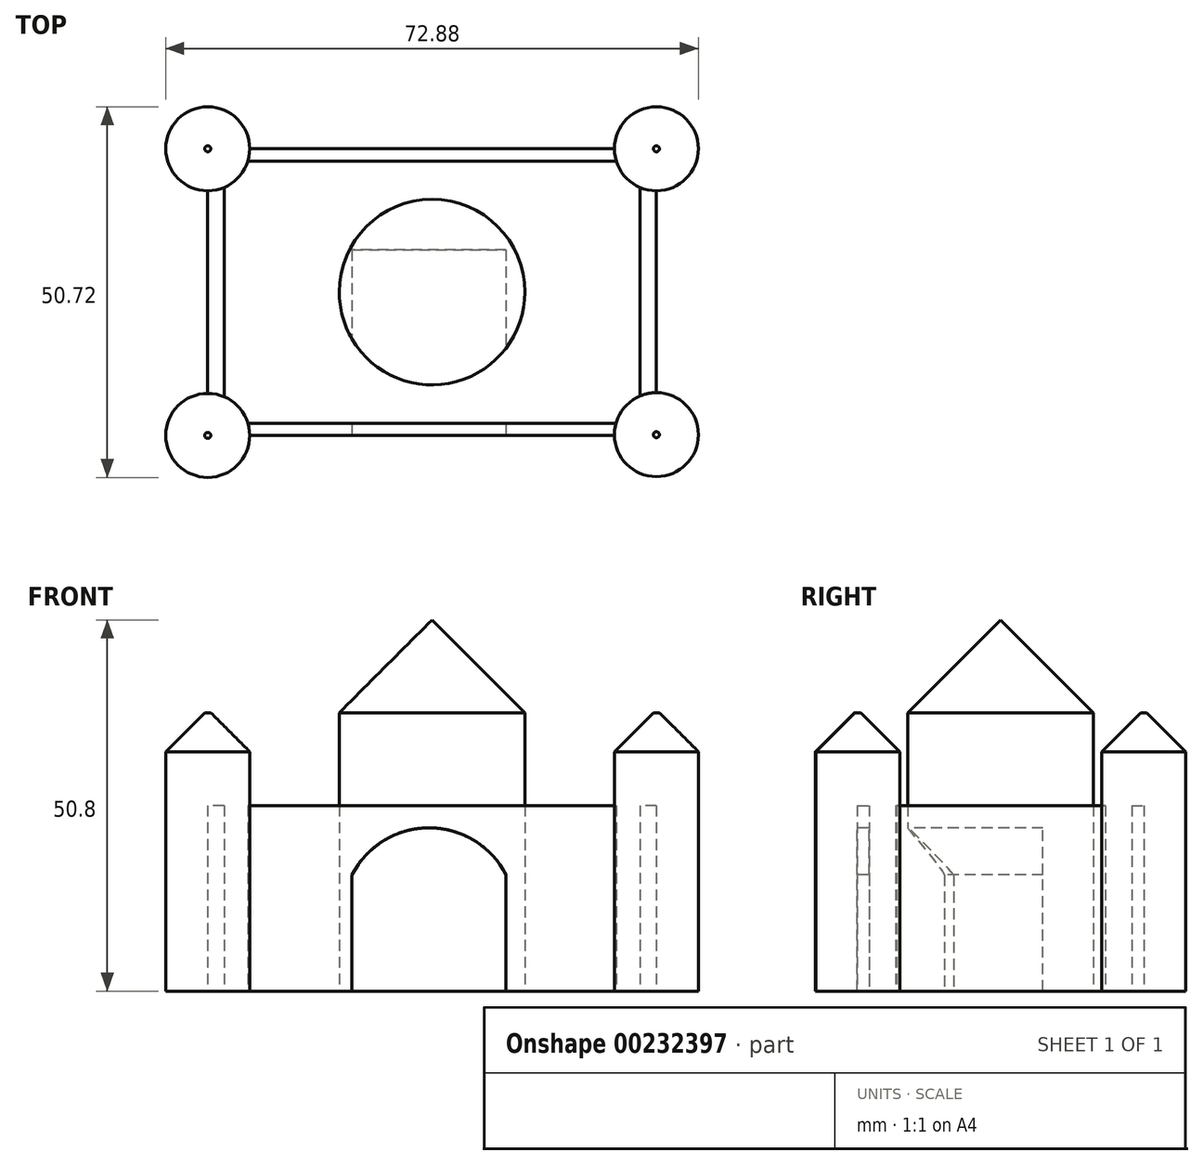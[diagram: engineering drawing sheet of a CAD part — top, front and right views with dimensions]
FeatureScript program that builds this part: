
annotation { "Feature Type Name" : "Feature", "Feature Type Description" : "" }
export const myFeature = defineFeature(function(context is Context, id is Id, definition is map)
    precondition{}
    {
        {
            var Q0;
            Q0=qCreatedBy(makeId("Top.planeOp"),FACE);
            var sketch = newSketch(context, id + "F0", { "sketchPlane" : qUnion([Q0])});
            skLineSegment(sketch, "E0.bottom", {"start": v(-24.95, -19.61) * mm, "end": v(24.95, -19.61) * mm});
            skLineSegment(sketch, "E0.top", {"start": v(-24.95, 19.61) * mm, "end": v(24.95, 19.61) * mm});
            skLineSegment(sketch, "E0.left", {"start": v(-30.7, -13.87) * mm, "end": v(-30.7, 13.87) * mm});
            skLineSegment(sketch, "E0.right", {"start": v(30.7, -19.61) * mm, "end": v(30.7, -19.52) * mm});
            skPoint(sketch, "E0.middle", {"position": v(0, 0) * mm});
            skCircle(sketch, "E1", {"center": v(0, 0) * mm, "radius": 12.7 * mm});
            skCircle(sketch, "E2", {"center": v(-30.7, 19.61) * mm, "radius": 5.75 * mm});
            skCircle(sketch, "E3", {"center": v(30.7, 19.61) * mm, "radius": 5.75 * mm});
            skCircle(sketch, "E4", {"center": v(30.7, -19.52) * mm, "radius": 5.75 * mm});
            skCircle(sketch, "E5", {"center": v(-30.7, -19.61) * mm, "radius": 5.75 * mm});
            skLineSegment(sketch, "E6.bottom", {"start": v(-25.2, -17.95) * mm, "end": v(25.17, -17.95) * mm});
            skLineSegment(sketch, "E6.top", {"start": v(-25.2, 17.95) * mm, "end": v(25.2, 17.95) * mm});
            skLineSegment(sketch, "E6.left", {"start": v(-28.44, -14.33) * mm, "end": v(-28.44, 14.33) * mm});
            skLineSegment(sketch, "E6.right", {"start": v(28.44, -14.23) * mm, "end": v(28.44, 14.33) * mm});
            skPoint(sketch, "E7.orphan", {"position": v(-28.44, -17.95) * mm});
            skLineSegment(sketch, "E8.trimOffspring", {"start": v(30.7, -13.77) * mm, "end": v(30.7, 13.87) * mm});
            skPoint(sketch, "E9.orphan", {"position": v(28.44, -17.95) * mm});
            skPoint(sketch, "E10.orphan", {"position": v(28.44, 17.95) * mm});
            skPoint(sketch, "E11.orphan", {"position": v(-28.44, 17.95) * mm});
            skSolve(sketch);
        }
        {
            var Q0;
            {var subQ0=sQuery(id+"F0.wireOp",EDGE,"E0.top");Q0=makeQuery(id+"F0.imprint","IMPRINT",FACE,{"disambiguationData":[TD([[makeQuery(id+"F0.imprint","IMPRINT",EDGE,{"derivedFrom":subQ0}),-1.0]])]});}
            var Q1;
            {var subQ0=sQuery(id+"F0.wireOp",EDGE,"E0.left");Q1=makeQuery(id+"F0.imprint","IMPRINT",FACE,{"disambiguationData":[TD([[makeQuery(id+"F0.imprint","IMPRINT",EDGE,{"derivedFrom":subQ0}),-1.0]])]});}
            var Q2;
            {var subQ0=sQuery(id+"F0.wireOp",EDGE,"E0.bottom");Q2=makeQuery(id+"F0.imprint","IMPRINT",FACE,{"disambiguationData":[TD([[makeQuery(id+"F0.imprint","IMPRINT",EDGE,{"derivedFrom":subQ0}),1.0]])]});}
            var Q3;
            {var subQ0=sQuery(id+"F0.wireOp",EDGE,"E6.right");Q3=makeQuery(id+"F0.imprint","IMPRINT",FACE,{"disambiguationData":[TD([[makeQuery(id+"F0.imprint","IMPRINT",EDGE,{"derivedFrom":subQ0}),-1.0]])]});}
            extrude(context, id + "F1", {"entities" : qUnion([Q0, Q1, Q2, Q3]), "depth" : 25.4 * mm});
        }
        {
            var Q0;
            {var subQ0=sQuery(id+"F0.wireOp",EDGE,"E2");var subQ1=makeQuery(id+"F0.imprint","INTERSECT",VERTEX,{"derivedFrom":[sQuery(id+"F0.wireOp",EDGE,"E0.top"),subQ0]});Q0=makeQuery(id+"F0.imprint","IMPRINT",FACE,{"disambiguationData":[TD([[makeQuery(id+"F0.imprint","IMPRINT",EDGE,{"disambiguationData":[TD([[subQ1,-1.0]])],"derivedFrom":subQ0}),1.0]])]});}
            var Q1;
            {var subQ0=sQuery(id+"F0.wireOp",EDGE,"E3");var subQ1=makeQuery(id+"F0.imprint","INTERSECT",VERTEX,{"derivedFrom":[sQuery(id+"F0.wireOp",EDGE,"E0.top"),subQ0]});Q1=makeQuery(id+"F0.imprint","IMPRINT",FACE,{"disambiguationData":[TD([[makeQuery(id+"F0.imprint","IMPRINT",EDGE,{"disambiguationData":[TD([[subQ1,-1.0]])],"derivedFrom":subQ0}),1.0]])]});}
            var Q2;
            {var subQ0=sQuery(id+"F0.wireOp",EDGE,"E5");var subQ1=makeQuery(id+"F0.imprint","INTERSECT",VERTEX,{"derivedFrom":[sQuery(id+"F0.wireOp",EDGE,"E0.bottom"),subQ0]});Q2=makeQuery(id+"F0.imprint","IMPRINT",FACE,{"disambiguationData":[TD([[makeQuery(id+"F0.imprint","IMPRINT",EDGE,{"disambiguationData":[TD([[subQ1,-1.0]])],"derivedFrom":subQ0}),1.0]])]});}
            var Q3;
            {var subQ0=sQuery(id+"F0.wireOp",EDGE,"E4");var subQ1=makeQuery(id+"F0.imprint","INTERSECT",VERTEX,{"derivedFrom":[subQ0,sQuery(id+"F0.wireOp",EDGE,"E6.right")]});Q3=makeQuery(id+"F0.imprint","IMPRINT",FACE,{"disambiguationData":[TD([[makeQuery(id+"F0.imprint","IMPRINT",EDGE,{"disambiguationData":[TD([[subQ1,1.0]])],"derivedFrom":subQ0}),1.0]])]});}
            extrude(context, id + "F2", {"entities" : qUnion([Q0, Q1, Q2, Q3]), "depth" : 38.1 * mm});
        }
        {
            var Q0;
            Q0=makeQuery(id+"F0.imprint","IMPRINT",FACE,{"disambiguationData":[TD([[makeQuery(id+"F0.imprint","IMPRINT",EDGE,{"derivedFrom":sQuery(id+"F0.wireOp",EDGE,"E1")}),1.0]])]});
            var Q1;
            Q1 = qSketchRegion(id + "F4", true);
            extrude(context, id + "F3", {"entities" : qUnion([Q0, Q1]), "depth" : 50.8 * mm});
        }
        {
            var Q0;
            Q0=makeQuery(id+"F1.opExtrude","SWEPT_FACE",FACE,{"disambiguationData":[OSD([sQuery(id+"F0.wireOp",EDGE,"E0.bottom")])]});
            var sketch = newSketch(context, id + "F4", { "sketchPlane" : qUnion([Q0])});
            skLineSegment(sketch, "E12.bottom", {"start": v(-10.96, 0) * mm, "end": v(10.13, 0) * mm});
            skLineSegment(sketch, "E12.left", {"start": v(-10.96, 0) * mm, "end": v(-10.96, 15.92) * mm});
            skLineSegment(sketch, "E12.right", {"start": v(10.13, 0) * mm, "end": v(10.13, 15.92) * mm});
            skArc(sketch, "E13", {"start": v(10.13, 15.92) * mm, "mid": v(-0.41, 22.34) * mm, "end": v(-10.96, 15.92) * mm});
            skSolve(sketch);
        }
        {
            var Q0;
            Q0 = qSketchRegion(id + "F4", true);
            extrude(context, id + "F5", {"entities" : qUnion([Q0]), "operationType" : NewBodyOperationType.REMOVE, "oppositeDirection" : true, "depth" : 25.4 * mm});
        }
        {
            var Q0;
            Q0=makeQuery(id+"F3.opExtrude","CAP_FACE",FACE,{"disambiguationData":[OSD([sQuery(id+"F0.wireOp",EDGE,"E1")])],"isStart":false});
            chamfer(context, id + "F6", {"entities" : qUnion([Q0]), "width" : 12.7 * mm, "tangentPropagation" : true});
        }
        {
            var Q0;
            Q0=makeQuery(id+"F2.opExtrude","CAP_FACE",FACE,{"disambiguationData":[OSD([sQuery(id+"F0.wireOp",EDGE,"E5")])],"isStart":false});
            var Q1;
            Q1=makeQuery(id+"F2.opExtrude","CAP_FACE",FACE,{"disambiguationData":[OSD([sQuery(id+"F0.wireOp",EDGE,"E4")])],"isStart":false});
            var Q2;
            Q2=makeQuery(id+"F2.opExtrude","CAP_FACE",FACE,{"disambiguationData":[OSD([sQuery(id+"F0.wireOp",EDGE,"E2")])],"isStart":false});
            var Q3;
            Q3=makeQuery(id+"F2.opExtrude","CAP_FACE",FACE,{"disambiguationData":[OSD([sQuery(id+"F0.wireOp",EDGE,"E3")])],"isStart":false});
            chamfer(context, id + "F7", {"entities" : qUnion([Q0, Q1, Q2, Q3]), "width" : 5.33 * mm, "tangentPropagation" : true});
        }
    });
